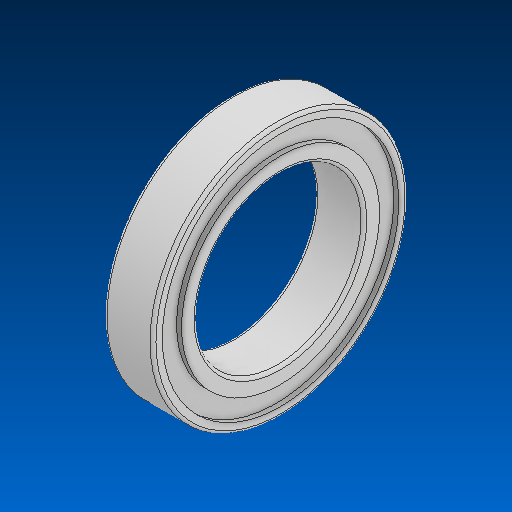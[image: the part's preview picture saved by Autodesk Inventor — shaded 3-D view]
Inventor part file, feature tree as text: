
AUTODESK INVENTOR PART (.ipt)
format: ipt  version: 2022.2 (Build 262287000, 287)  size: 180,736 bytes
history: native  units: in
note: dims shown in document units (in); Inventor stores cm internally (conversion verified against a paired STEP export)
features: fillet x1
ambient origin geometry x8: Origin, YZ Plane, XZ Plane, XY Plane, X Axis, Y Axis, Z Axis, Center Point
bodies: Solid1 (feature_tree)
feature tree (1):
  fillet  "Fillet1"  [1 undecoded]
note: 1 required parameter value undecoded (feature->parameter linkage not recoverable at this tier; creation-order binding heuristic only, values carry confidence <= 0.55)
